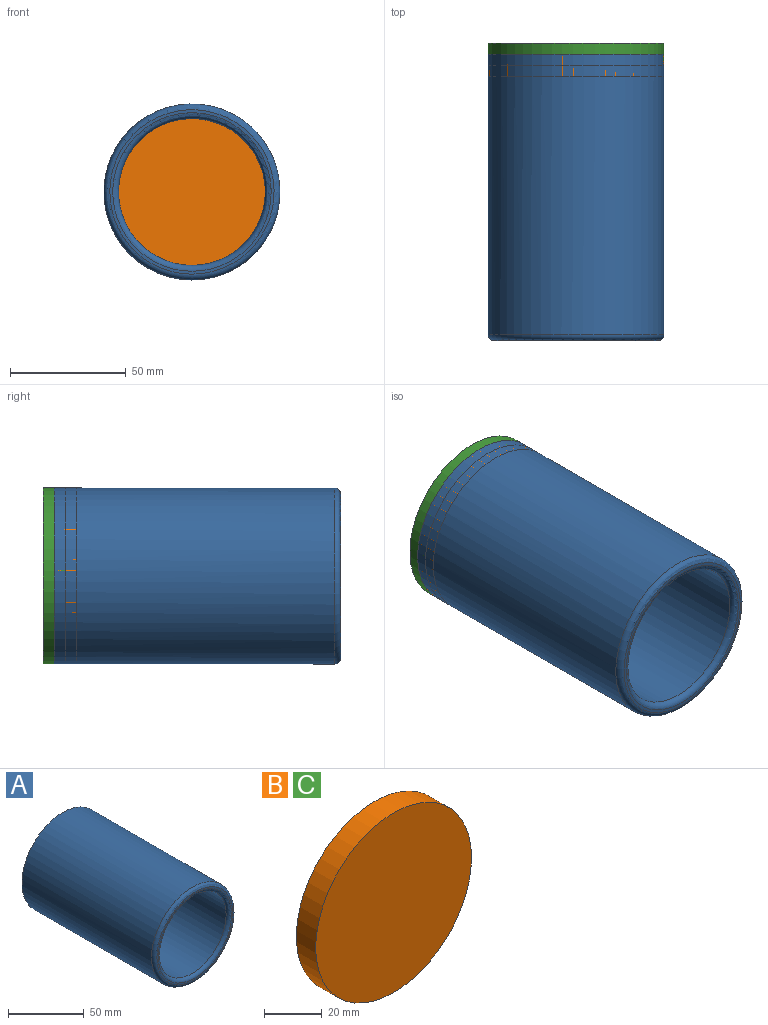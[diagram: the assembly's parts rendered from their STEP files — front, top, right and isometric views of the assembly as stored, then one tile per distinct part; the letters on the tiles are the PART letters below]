
ASSEMBLY  parts=3 mates=1
PART A: 6 faces, bbox 82.5x123.8x82.5 mm
  f0: cylinder r=31.75mm len=121.29mm, axis (0,1,0), area 24195.3mm2, adj f3,f4
  f1: cylinder r=38.1mm len=121.29mm, axis (0,1,0), area 29034.3mm2, adj f3,f5
  f2: plane 71.12x71.12mm, normal (0,-1,0), area 278.7mm2, adj f4,f5
  f3: plane 76.2x76.2mm, normal (0,1,0), area 1393.4mm2, adj f0,f1
  f4: torus R=34.29mm, axis (0,-1,0), area 819.1mm2, adj f0,f2
  f5: torus R=35.56mm, axis (0,-1,0), area 932mm2, adj f1,f2
PART B: 3 faces, bbox 76.2x9.5x76.2 mm
  f0: cylinder r=38.1mm len=76.2mm, axis (0,1,0), area 2280.2mm2, adj f1,f2
  f1: plane 76.2x76.2mm, normal (0,-1,0), area 4560.4mm2, adj f0
  f2: plane 76.2x76.2mm, normal (0,1,0), area 4560.4mm2, adj f0
PART C: same geometry as B
PLACE A t=(-49.53,-29.73,-8.84)mm
PLACE B t=(-49.53,-29.73,-8.84)mm
PLACE C t=(-49.53,-24.96,-8.84)mm
MATE fastened C.f0 <-> A.f0  axis (0,1,0) through (-49.53,-29.73,-8.84)mm
